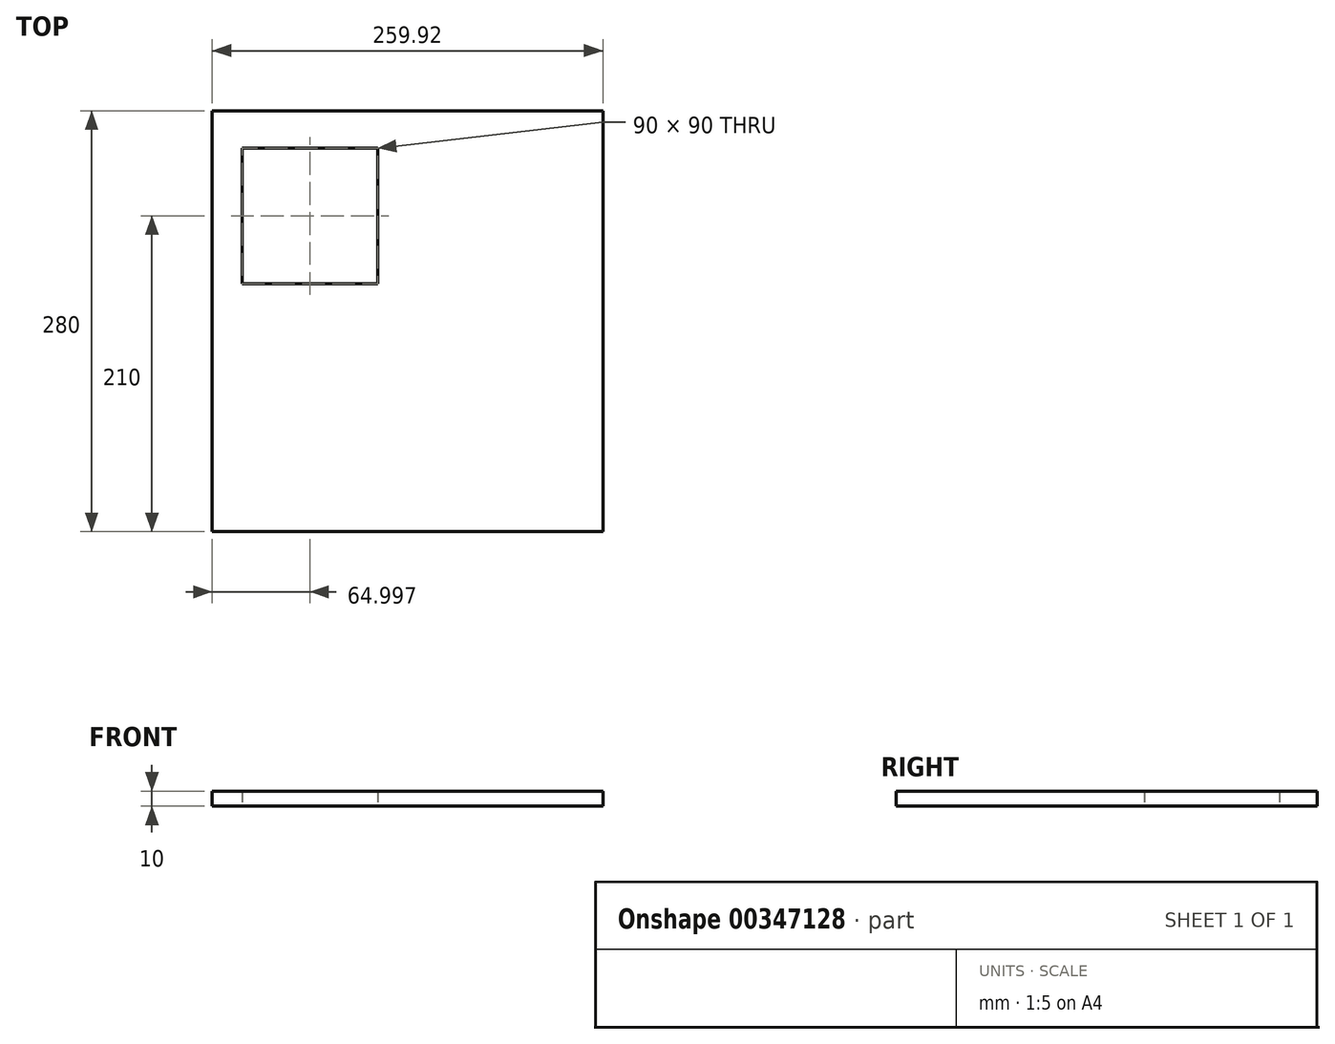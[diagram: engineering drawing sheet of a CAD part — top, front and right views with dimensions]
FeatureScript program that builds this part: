
annotation { "Feature Type Name" : "Feature", "Feature Type Description" : "" }
export const myFeature = defineFeature(function(context is Context, id is Id, definition is map)
    precondition{}
    {
        {
            var Q0;
            Q0=qCreatedBy(makeId("Top.planeOp"),FACE);
            var sketch = newSketch(context, id + "F0", { "sketchPlane" : qUnion([Q0])});
            skLineSegment(sketch, "E0.bottom", {"start": v(-129.96, 140) * mm, "end": v(129.96, 140) * mm});
            skLineSegment(sketch, "E0.top", {"start": v(-129.96, -140) * mm, "end": v(129.96, -140) * mm});
            skLineSegment(sketch, "E0.left", {"start": v(-129.96, 140) * mm, "end": v(-129.96, -140) * mm});
            skLineSegment(sketch, "E0.right", {"start": v(129.96, 140) * mm, "end": v(129.96, -140) * mm});
            skPoint(sketch, "E0.middle", {"position": v(0, 0) * mm});
            skPoint(sketch, "E1.visualSharp", {"position": v(-129.96, 140) * mm});
            skLineSegment(sketch, "E1.filletArc", {"start": v(-129.96, 140) * mm, "end": v(-129.96, 140) * mm});
            skPoint(sketch, "E2.visualSharp", {"position": v(129.96, 140) * mm});
            skLineSegment(sketch, "E2.filletArc", {"start": v(129.96, 140) * mm, "end": v(129.96, 140) * mm});
            skPoint(sketch, "E3.visualSharp", {"position": v(129.96, -140) * mm});
            skLineSegment(sketch, "E3.filletArc", {"start": v(129.96, -140) * mm, "end": v(129.96, -140) * mm});
            skPoint(sketch, "E4.visualSharp", {"position": v(-129.96, -140) * mm});
            skLineSegment(sketch, "E4.filletArc", {"start": v(-129.96, -140) * mm, "end": v(-129.96, -140) * mm});
            skPoint(sketch, "E5.middle", {"position": v(-59.96, 70) * mm});
            skLineSegment(sketch, "E6.bottom", {"start": v(-109.96, 115) * mm, "end": v(-19.96, 115) * mm});
            skLineSegment(sketch, "E6.top", {"start": v(-109.96, 25) * mm, "end": v(-19.96, 25) * mm});
            skLineSegment(sketch, "E6.left", {"start": v(-109.96, 115) * mm, "end": v(-109.96, 25) * mm});
            skLineSegment(sketch, "E6.right", {"start": v(-19.96, 115) * mm, "end": v(-19.96, 25) * mm});
            skPoint(sketch, "E6.middle", {"position": v(-64.96, 70) * mm});
            skSolve(sketch);
        }
        {
            var Q0;
            Q0=qSketchRegion(id+"F0",true);
            extrude(context, id + "F1", {"entities" : qUnion([Q0]), "depth" : 10 * mm});
        }
    });
